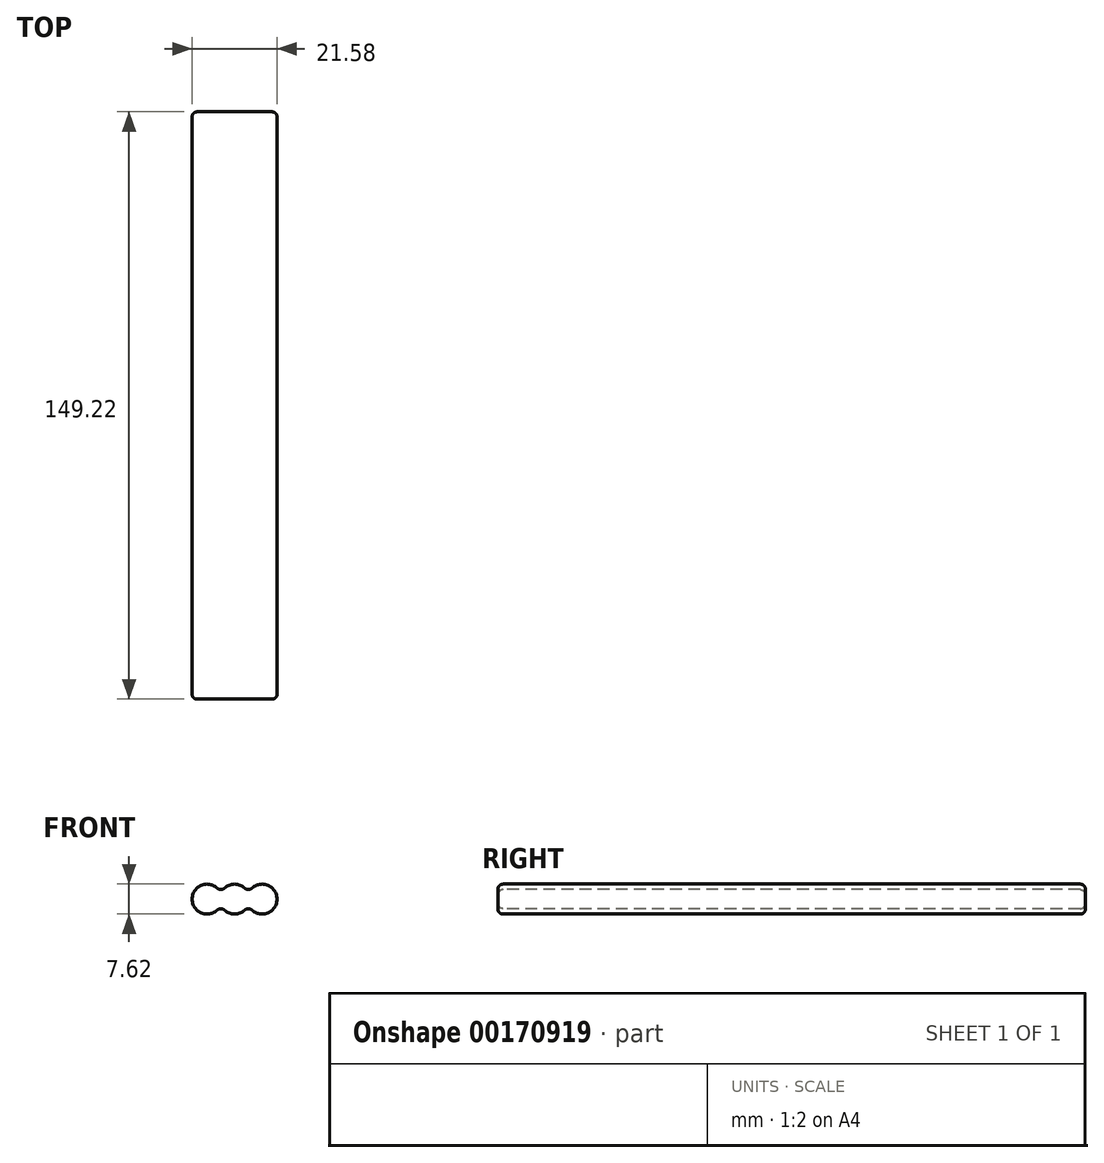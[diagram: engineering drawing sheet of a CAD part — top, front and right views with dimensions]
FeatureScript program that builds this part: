
annotation { "Feature Type Name" : "Feature", "Feature Type Description" : "" }
export const myFeature = defineFeature(function(context is Context, id is Id, definition is map)
    precondition{}
    {
        {
            var Q0;
            Q0=qCreatedBy(makeId("Front.planeOp"),FACE);
            var sketch = newSketch(context, id + "F0", { "sketchPlane" : qUnion([Q0])});
            skArc(sketch, "E0", {"start": v(3.5, 1.52) * mm, "mid": v(0, 3.81) * mm, "end": v(-3.5, 1.52) * mm});
            skArc(sketch, "E1", {"start": v(3.5, -1.52) * mm, "mid": v(10.8, 0) * mm, "end": v(3.5, 1.52) * mm});
            skArc(sketch, "E2", {"start": v(-3.5, 1.52) * mm, "mid": v(-10.8, 0) * mm, "end": v(-3.5, -1.52) * mm});
            skLineSegment(sketch, "E3", {"start": v(-6.99, 0) * mm, "end": v(6.99, 0) * mm, "construction": true});
            skArc(sketch, "E4.trimOffspring", {"start": v(-3.5, -1.52) * mm, "mid": v(0, -3.81) * mm, "end": v(3.5, -1.52) * mm});
            skSolve(sketch);
        }
        {
            var Q0;
            Q0=makeQuery(id+"F0.imprint","IMPRINT",FACE,{"disambiguationData":[TD([[makeQuery(id+"F0.imprint","IMPRINT",EDGE,{"derivedFrom":sQuery(id+"F0.wireOp",EDGE,"E0")}),1.0]])]});
            extrude(context, id + "F1", {"entities" : qUnion([Q0]), "depth" : 149.22 * mm, "symmetric" : true});
        }
        {
            var Q0;
            Q0=makeQuery(id+"F1.opExtrude","SWEPT_EDGE",EDGE,{"disambiguationData":[OSD([sQuery(id+"F0.wireOp",EDGE,"E0"),sQuery(id+"F0.wireOp",EDGE,"E2")])]});
            var Q1;
            Q1=makeQuery(id+"F1.opExtrude","SWEPT_EDGE",EDGE,{"disambiguationData":[OSD([sQuery(id+"F0.wireOp",EDGE,"E0"),sQuery(id+"F0.wireOp",EDGE,"E1")])]});
            var Q2;
            Q2=makeQuery(id+"F1.opExtrude","SWEPT_EDGE",EDGE,{"disambiguationData":[OSD([sQuery(id+"F0.wireOp",EDGE,"E2"),sQuery(id+"F0.wireOp",EDGE,"E4.trimOffspring")])]});
            var Q3;
            Q3=makeQuery(id+"F1.opExtrude","SWEPT_EDGE",EDGE,{"disambiguationData":[OSD([sQuery(id+"F0.wireOp",EDGE,"E1"),sQuery(id+"F0.wireOp",EDGE,"E4.trimOffspring")])]});
            var Q4;
            Q4=makeQuery(id+"F1.opExtrude","CAP_FACE",FACE,{"disambiguationData":[OSD([sQuery(id+"F0.wireOp",EDGE,"E0"),sQuery(id+"F0.wireOp",EDGE,"E1"),sQuery(id+"F0.wireOp",EDGE,"E2"),sQuery(id+"F0.wireOp",EDGE,"E4.trimOffspring")])],"isStart":true});
            var Q5;
            Q5=makeQuery(id+"F1.opExtrude","CAP_FACE",FACE,{"disambiguationData":[OSD([sQuery(id+"F0.wireOp",EDGE,"E0"),sQuery(id+"F0.wireOp",EDGE,"E1"),sQuery(id+"F0.wireOp",EDGE,"E2"),sQuery(id+"F0.wireOp",EDGE,"E4.trimOffspring")])],"isStart":false});
            fillet(context, id + "F2", {"entities" : qUnion([Q0, Q1, Q2, Q3, Q4, Q5]), "radius" : 1.27 * mm, "tangentPropagation" : true, "allowEdgeOverflow" : false});
        }
    });
